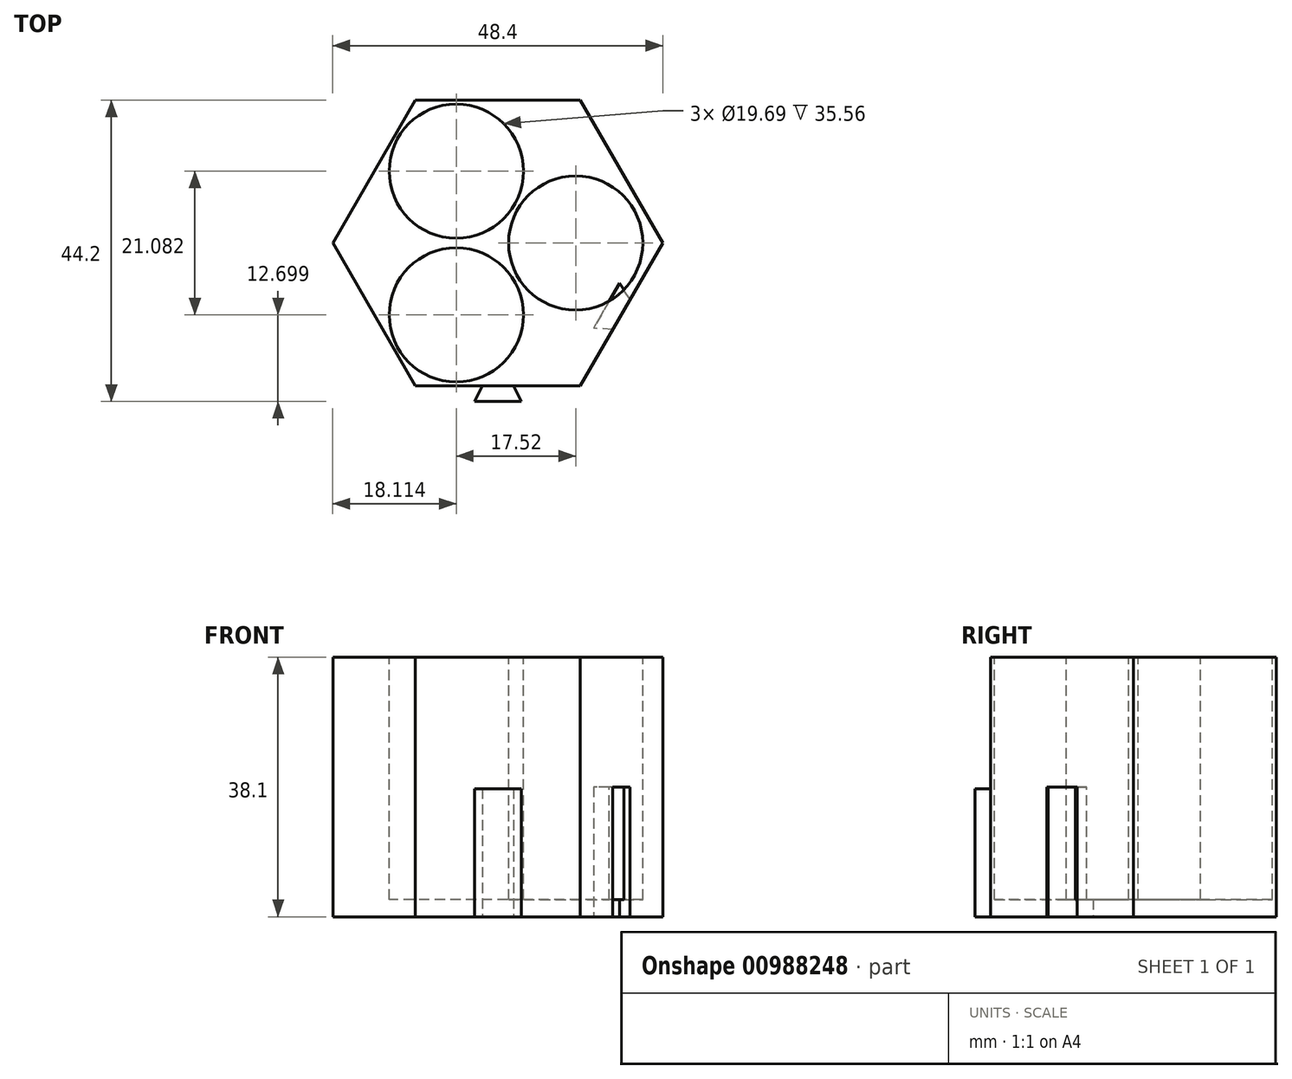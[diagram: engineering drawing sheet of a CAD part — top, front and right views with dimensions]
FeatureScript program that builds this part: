
annotation { "Feature Type Name" : "Feature", "Feature Type Description" : "" }
export const myFeature = defineFeature(function(context is Context, id is Id, definition is map)
    precondition{}
    {
        {
            var Q0;
            Q0=qCreatedBy(makeId("Top.planeOp"),FACE);
            var sketch = newSketch(context, id + "F0", { "sketchPlane" : qUnion([Q0])});
            skCircle(sketch, "E0.cCircle", {"center": v(0, 0) * mm, "radius": 20.96 * mm, "construction": true});
            skLineSegment(sketch, "E0.0", {"start": v(12.1, -20.96) * mm, "end": v(-12.1, -20.96) * mm});
            skLineSegment(sketch, "E0.1", {"start": v(-12.1, -20.96) * mm, "end": v(-24.2, 0) * mm});
            skLineSegment(sketch, "E0.2", {"start": v(-24.2, 0) * mm, "end": v(-12.1, 20.95) * mm});
            skLineSegment(sketch, "E0.3", {"start": v(-12.1, 20.95) * mm, "end": v(12.1, 20.96) * mm});
            skLineSegment(sketch, "E0.4", {"start": v(12.1, 20.96) * mm, "end": v(24.2, 0) * mm});
            skLineSegment(sketch, "E0.5", {"start": v(24.2, 0) * mm, "end": v(12.1, -20.96) * mm});
            skPoint(sketch, "E0.0.midPoint", {"position": v(0, -20.96) * mm});
            skSolve(sketch);
        }
        {
            var Q0;
            Q0 = qSketchRegion(id + "F0", true);
            extrude(context, id + "F1", {"entities" : qUnion([Q0]), "depth" : 38.1 * mm, "offsetDistance" : 25.4 * mm});
        }
        {
            var Q0;
            Q0=makeQuery(id+"F1.opExtrude","CAP_FACE",FACE,{"disambiguationData":[OSD([sQuery(id+"F0.wireOp",EDGE,"E0.0"),sQuery(id+"F0.wireOp",EDGE,"E0.1"),sQuery(id+"F0.wireOp",EDGE,"E0.2"),sQuery(id+"F0.wireOp",EDGE,"E0.3"),sQuery(id+"F0.wireOp",EDGE,"E0.4"),sQuery(id+"F0.wireOp",EDGE,"E0.5")])],"isStart":true});
            var sketch = newSketch(context, id + "F2", { "sketchPlane" : qUnion([Q0])});
            skLineSegment(sketch, "E1", {"start": v(0, 20.96) * mm, "end": v(0, 23.24) * mm});
            skLineSegment(sketch, "E2", {"start": v(0, 20.96) * mm, "end": v(-2.29, 20.96) * mm});
            skLineSegment(sketch, "E3", {"start": v(0, 23.24) * mm, "end": v(-3.43, 23.24) * mm});
            skLineSegment(sketch, "E4", {"start": v(-3.43, 23.24) * mm, "end": v(-2.29, 20.96) * mm});
            skLineSegment(sketch, "E5.MirrorCS", {"start": v(0, 23.24) * mm, "end": v(3.43, 23.24) * mm});
            skLineSegment(sketch, "E6.MirrorCS", {"start": v(3.43, 23.24) * mm, "end": v(2.29, 20.96) * mm});
            skLineSegment(sketch, "E7.MirrorCS", {"start": v(0, 20.96) * mm, "end": v(2.29, 20.96) * mm});
            skSolve(sketch);
        }
        {
            var Q0;
            Q0 = qSketchRegion(id + "F2", true);
            extrude(context, id + "F3", {"entities" : qUnion([Q0]), "operationType" : NewBodyOperationType.ADD, "oppositeDirection" : true, "depth" : 18.8 * mm, "offsetDistance" : 25.4 * mm});
        }
        {
            var Q0;
            Q0=makeQuery(id+"F3.boolean.opBoolean","MERGE",FACE,{"derivedFrom":[makeQuery(id+"F1.opExtrude","CAP_FACE",FACE,{"disambiguationData":[OSD([sQuery(id+"F0.wireOp",EDGE,"E0.0"),sQuery(id+"F0.wireOp",EDGE,"E0.1"),sQuery(id+"F0.wireOp",EDGE,"E0.2"),sQuery(id+"F0.wireOp",EDGE,"E0.3"),sQuery(id+"F0.wireOp",EDGE,"E0.4"),sQuery(id+"F0.wireOp",EDGE,"E0.5")])],"isStart":true}),makeQuery(id+"F3.opExtrude","CAP_FACE",FACE,{"disambiguationData":[OSD([sQuery(id+"F2.wireOp",EDGE,"E2"),sQuery(id+"F2.wireOp",EDGE,"E3"),sQuery(id+"F2.wireOp",EDGE,"E4"),sQuery(id+"F2.wireOp",EDGE,"E5.MirrorCS"),sQuery(id+"F2.wireOp",EDGE,"E6.MirrorCS"),sQuery(id+"F2.wireOp",EDGE,"E7.MirrorCS")])],"isStart":true})]});
            var sketch = newSketch(context, id + "F4", { "sketchPlane" : qUnion([Q0])});
            skLineSegment(sketch, "E8", {"start": v(18.15, 10.48) * mm, "end": v(-18.15, -10.48) * mm});
            skLineSegment(sketch, "E9", {"start": v(18.15, 10.48) * mm, "end": v(15.95, 9.2) * mm});
            skLineSegment(sketch, "E10", {"start": v(15.95, 9.2) * mm, "end": v(14.04, 12.5) * mm});
            skLineSegment(sketch, "E11", {"start": v(18.15, 10.48) * mm, "end": v(16.88, 12.68) * mm});
            skLineSegment(sketch, "E12", {"start": v(16.88, 12.68) * mm, "end": v(14.04, 12.5) * mm});
            skLineSegment(sketch, "E13.MirrorCS", {"start": v(15.95, 9.2) * mm, "end": v(17.85, 5.9) * mm});
            skLineSegment(sketch, "E14.MirrorCS", {"start": v(19.42, 8.28) * mm, "end": v(17.85, 5.9) * mm});
            skLineSegment(sketch, "E15.MirrorCS", {"start": v(18.15, 10.48) * mm, "end": v(19.42, 8.28) * mm});
            skSolve(sketch);
        }
        {
            var Q0;
            {var subQ0=sQuery(id+"F4.wireOp",EDGE,"E13.MirrorCS");var subQ1=sQuery(id+"F4.wireOp",EDGE,"E10");Q0=qUnion([makeQuery(id+"F4.imprint","IMPRINT",FACE,{"disambiguationData":[TD([[makeQuery(id+"F4.imprint","IMPRINT",EDGE,{"derivedFrom":subQ1}),-1.0]])]}),makeQuery(id+"F4.imprint","IMPRINT",FACE,{"disambiguationData":[TD([[makeQuery(id+"F4.imprint","IMPRINT",EDGE,{"derivedFrom":subQ0}),1.0]])]})]);}
            extrude(context, id + "F5", {"entities" : qUnion([Q0]), "operationType" : NewBodyOperationType.REMOVE, "oppositeDirection" : true, "depth" : 19.05 * mm, "offsetDistance" : 25.4 * mm});
        }
        {
            var Q0;
            Q0=makeQuery(id+"F1.opExtrude","CAP_FACE",FACE,{"disambiguationData":[OSD([sQuery(id+"F0.wireOp",EDGE,"E0.0"),sQuery(id+"F0.wireOp",EDGE,"E0.1"),sQuery(id+"F0.wireOp",EDGE,"E0.2"),sQuery(id+"F0.wireOp",EDGE,"E0.3"),sQuery(id+"F0.wireOp",EDGE,"E0.4"),sQuery(id+"F0.wireOp",EDGE,"E0.5")])],"isStart":false});
            var sketch = newSketch(context, id + "F6", { "sketchPlane" : qUnion([Q0])});
            skCircle(sketch, "E16", {"center": v(-6.09, 10.54) * mm, "radius": 9.84 * mm});
            skCircle(sketch, "E17", {"center": v(-6.09, -10.54) * mm, "radius": 9.84 * mm});
            skCircle(sketch, "E18", {"center": v(11.43, 0) * mm, "radius": 9.84 * mm});
            skSolve(sketch);
        }
        {
            var Q0;
            Q0=makeQuery(id+"F6.imprint","IMPRINT",FACE,{"disambiguationData":[TD([[makeQuery(id+"F6.imprint","IMPRINT",EDGE,{"derivedFrom":sQuery(id+"F6.wireOp",EDGE,"E17")}),1.0]])]});
            var Q1;
            Q1=makeQuery(id+"F6.imprint","IMPRINT",FACE,{"disambiguationData":[TD([[makeQuery(id+"F6.imprint","IMPRINT",EDGE,{"derivedFrom":sQuery(id+"F6.wireOp",EDGE,"E16")}),1.0]])]});
            var Q2;
            Q2=makeQuery(id+"F6.imprint","IMPRINT",FACE,{"disambiguationData":[TD([[makeQuery(id+"F6.imprint","IMPRINT",EDGE,{"derivedFrom":sQuery(id+"F6.wireOp",EDGE,"E18")}),1.0]])]});
            extrude(context, id + "F7", {"entities" : qUnion([Q0, Q1, Q2]), "operationType" : NewBodyOperationType.REMOVE, "oppositeDirection" : true, "depth" : 35.56 * mm, "offsetDistance" : 25.4 * mm});
        }
    });
